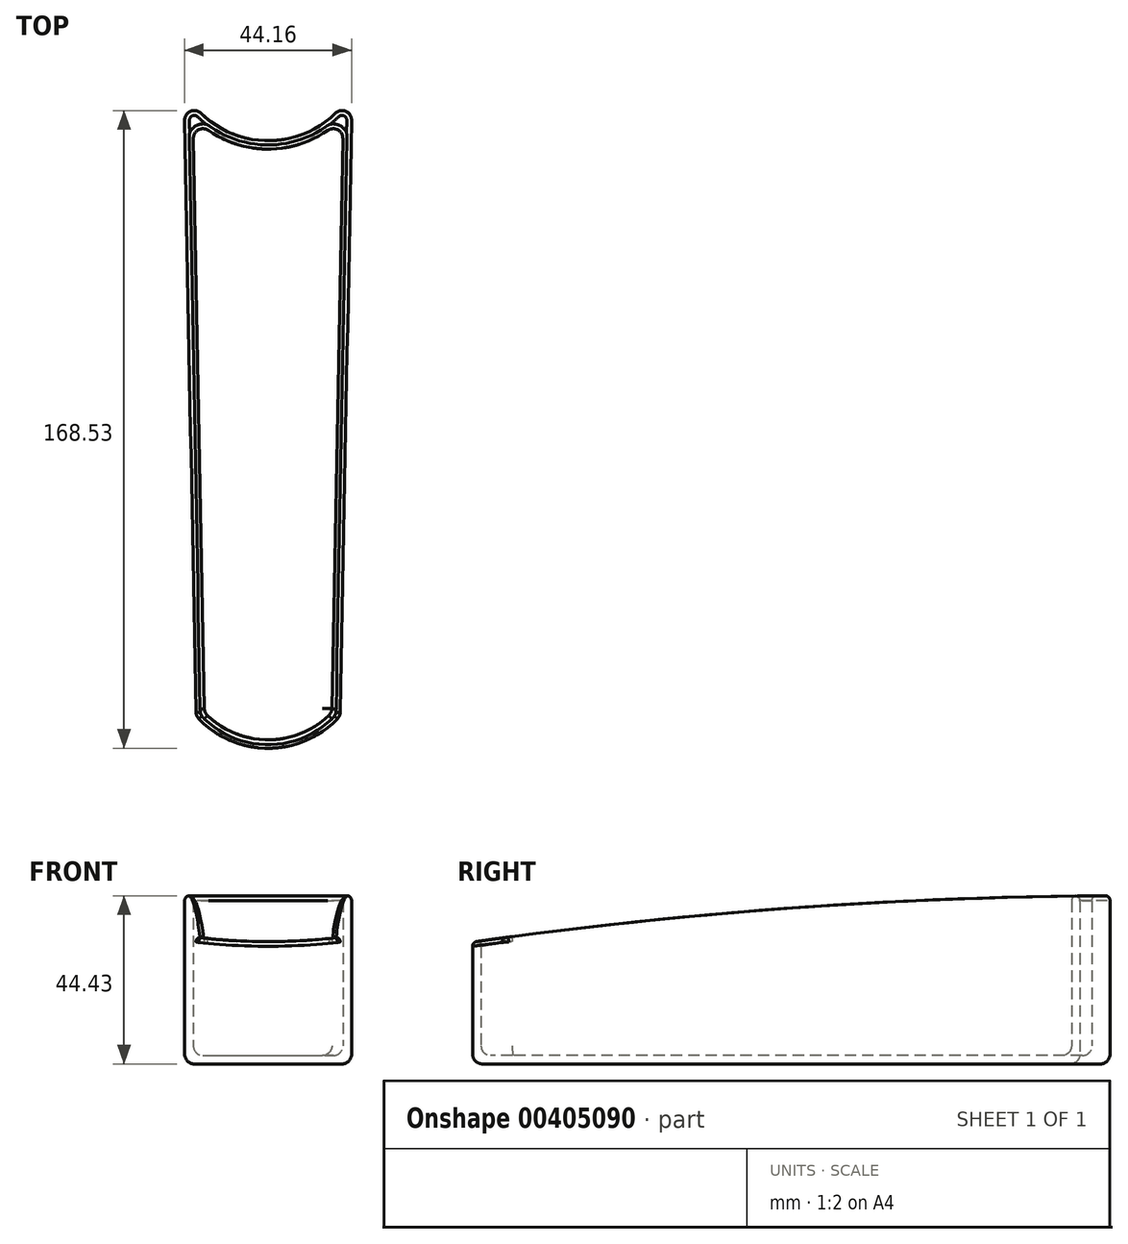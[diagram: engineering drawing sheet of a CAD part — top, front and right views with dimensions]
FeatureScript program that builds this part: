
annotation { "Feature Type Name" : "Feature", "Feature Type Description" : "" }
export const myFeature = defineFeature(function(context is Context, id is Id, definition is map)
    precondition{}
    {
        {
            var Q0;
            Q0=qCreatedBy(makeId("Top.planeOp"),FACE);
            var sketch = newSketch(context, id + "F0", { "sketchPlane" : qUnion([Q0])});
            skLineSegment(sketch, "E0", {"start": v(0, 76.2) * mm, "end": v(0, -76.2) * mm, "construction": true});
            skLineSegment(sketch, "E1", {"start": v(-22.23, 63.47) * mm, "end": v(0, 63.47) * mm, "construction": true});
            skLineSegment(sketch, "E2", {"start": v(0, -101.6) * mm, "end": v(-19.05, -101.6) * mm, "construction": true});
            skLineSegment(sketch, "E3", {"start": v(-22.23, 63.47) * mm, "end": v(-19.05, -101.6) * mm});
            skArc(sketch, "E4", {"start": v(-19.05, -101.6) * mm, "mid": v(-10.45, -107.95) * mm, "end": v(0, -110.2) * mm});
            skLineSegment(sketch, "E5", {"start": v(0, -110.2) * mm, "end": v(27.93, -110.2) * mm, "construction": true});
            skArc(sketch, "E6", {"start": v(-22.22, 63.47) * mm, "mid": v(-12.9, 53.89) * mm, "end": v(0, 50.37) * mm});
            skLineSegment(sketch, "E7", {"start": v(0, 50.37) * mm, "end": v(33.83, 50.37) * mm, "construction": true});
            skArc(sketch, "E8.MirrorCS", {"start": v(22.22, 63.47) * mm, "mid": v(12.9, 53.89) * mm, "end": v(0, 50.37) * mm});
            skLineSegment(sketch, "E9.MirrorCS", {"start": v(22.22, 63.47) * mm, "end": v(19.05, -101.6) * mm});
            skArc(sketch, "E10.MirrorCS", {"start": v(19.05, -101.6) * mm, "mid": v(10.45, -107.95) * mm, "end": v(0, -110.2) * mm});
            skArc(sketch, "E11.0", {"start": v(-19.54, 55.8) * mm, "mid": v(-10.55, 49.9) * mm, "end": v(0, 47.83) * mm, "construction": true});
            skArc(sketch, "E11.1", {"start": v(-16.53, -100.6) * mm, "mid": v(-8.99, -105.82) * mm, "end": v(0, -107.66) * mm, "construction": true});
            skArc(sketch, "E11.2", {"start": v(16.53, -100.6) * mm, "mid": v(8.99, -105.82) * mm, "end": v(0, -107.66) * mm, "construction": true});
            skLineSegment(sketch, "E11.3", {"start": v(-19.54, 55.8) * mm, "end": v(-16.53, -100.6) * mm, "construction": true});
            skLineSegment(sketch, "E11.4", {"start": v(19.54, 55.8) * mm, "end": v(16.53, -100.6) * mm, "construction": true});
            skArc(sketch, "E11.5", {"start": v(19.54, 55.8) * mm, "mid": v(10.55, 49.9) * mm, "end": v(0, 47.83) * mm, "construction": true});
            skCircle(sketch, "E12", {"center": v(0, 76.2) * mm, "radius": 22.86 * mm, "construction": true});
            skSolve(sketch);
        }
        {
            var Q0;
            Q0 = qSketchRegion(id + "F0", true);
            extrude(context, id + "F1", {"entities" : qUnion([Q0]), "depth" : 50.8 * mm, "offsetDistance" : 25.4 * mm});
        }
        {
            var Q0;
            Q0=qCreatedBy(makeId("Right.planeOp"),FACE);
            var sketch = newSketch(context, id + "F2", { "sketchPlane" : qUnion([Q0])});
            skArc(sketch, "E13", {"start": v(63.79, 44.45) * mm, "mid": v(-25.02, 41.27) * mm, "end": v(-113.37, 31.75) * mm});
            skLineSegment(sketch, "E14", {"start": v(63.79, 44.45) * mm, "end": v(63.79, 69.85) * mm});
            skLineSegment(sketch, "E15", {"start": v(63.79, 69.85) * mm, "end": v(-113.37, 69.85) * mm});
            skLineSegment(sketch, "E16", {"start": v(-113.37, 69.85) * mm, "end": v(-113.37, 31.75) * mm});
            skPoint(sketch, "E17.0", {"position": v(63.47, 0) * mm});
            skPoint(sketch, "E17.1", {"position": v(-110.2, 0) * mm});
            skLineSegment(sketch, "E18", {"start": v(63.79, 44.45) * mm, "end": v(76.14, 44.45) * mm, "construction": true});
            skSolve(sketch);
        }
        {
            var Q0;
            Q0=makeQuery(id+"F2.imprint","IMPRINT",FACE,{"disambiguationData":[TD([[makeQuery(id+"F2.imprint","IMPRINT",EDGE,{"derivedFrom":sQuery(id+"F2.wireOp",EDGE,"E13")}),-1.0]])]});
            extrude(context, id + "F3", {"entities" : qUnion([Q0]), "operationType" : NewBodyOperationType.REMOVE, "endBound" : BoundingType.THROUGH_ALL, "oppositeDirection" : true, "depth" : 25.4 * mm, "offsetDistance" : 25.4 * mm, "hasSecondDirection" : true, "secondDirectionBound" : SecondDirectionBoundingType.THROUGH_ALL, "secondDirectionOppositeDirection" : false, "secondDirectionDepth" : 25.4 * mm});
        }
        {
            var Q0;
            Q0=makeQuery(id+"F3.boolean.opBoolean","COPY",FACE,{"derivedFrom":makeQuery(id+"F3.opExtrude","SWEPT_FACE",FACE,{"disambiguationData":[OSD([sQuery(id+"F2.wireOp",EDGE,"E13")])]})});
            shell(context, id + "F4", {"entities" : qUnion([Q0]), "thickness" : 2.22 * mm});
        }
        {
            var Q0;
            Q0=makeQuery(id+"F4.opShell","OFFSET_FACE",FACE,{"disambiguationData":[OSD([sQuery(id+"F0.wireOp",EDGE,"E3"),sQuery(id+"F0.wireOp",EDGE,"E4"),sQuery(id+"F0.wireOp",EDGE,"E6"),sQuery(id+"F0.wireOp",EDGE,"E8.MirrorCS"),sQuery(id+"F0.wireOp",EDGE,"E9.MirrorCS"),sQuery(id+"F0.wireOp",EDGE,"E10.MirrorCS")])]});
            var Q1;
            Q1=makeQuery(id+"F4.opShell","OFFSET_EDGE",EDGE,{"disambiguationData":[OSD([sQuery(id+"F0.wireOp",EDGE,"E3"),sQuery(id+"F0.wireOp",EDGE,"E4")])]});
            var Q2;
            Q2=makeQuery(id+"F4.opShell","OFFSET_EDGE",EDGE,{"disambiguationData":[OSD([sQuery(id+"F0.wireOp",EDGE,"E3"),sQuery(id+"F0.wireOp",EDGE,"E6")])]});
            var Q3;
            Q3=makeQuery(id+"F4.opShell","OFFSET_EDGE",EDGE,{"disambiguationData":[OSD([sQuery(id+"F0.wireOp",EDGE,"E8.MirrorCS"),sQuery(id+"F0.wireOp",EDGE,"E9.MirrorCS")])]});
            var Q4;
            Q4=makeQuery(id+"F4.opShell","OFFSET_EDGE",EDGE,{"disambiguationData":[OSD([sQuery(id+"F0.wireOp",EDGE,"E9.MirrorCS"),sQuery(id+"F0.wireOp",EDGE,"E10.MirrorCS")])]});
            var Q5;
            Q5=makeQuery(id+"F1.opExtrude","SWEPT_EDGE",EDGE,{"disambiguationData":[OSD([sQuery(id+"F0.wireOp",EDGE,"E3"),sQuery(id+"F0.wireOp",EDGE,"E6")])]});
            var Q6;
            Q6=makeQuery(id+"F1.opExtrude","SWEPT_EDGE",EDGE,{"disambiguationData":[OSD([sQuery(id+"F0.wireOp",EDGE,"E8.MirrorCS"),sQuery(id+"F0.wireOp",EDGE,"E9.MirrorCS")])]});
            var Q7;
            Q7=makeQuery(id+"F1.opExtrude","CAP_FACE",FACE,{"disambiguationData":[OSD([sQuery(id+"F0.wireOp",EDGE,"E3"),sQuery(id+"F0.wireOp",EDGE,"E4"),sQuery(id+"F0.wireOp",EDGE,"E6"),sQuery(id+"F0.wireOp",EDGE,"E8.MirrorCS"),sQuery(id+"F0.wireOp",EDGE,"E9.MirrorCS"),sQuery(id+"F0.wireOp",EDGE,"E10.MirrorCS")])],"isStart":true});
            var Q8;
            Q8=makeQuery(id+"F1.opExtrude","SWEPT_EDGE",EDGE,{"disambiguationData":[OSD([sQuery(id+"F0.wireOp",EDGE,"E3"),sQuery(id+"F0.wireOp",EDGE,"E4")])]});
            var Q9;
            Q9=makeQuery(id+"F1.opExtrude","SWEPT_EDGE",EDGE,{"disambiguationData":[OSD([sQuery(id+"F0.wireOp",EDGE,"E9.MirrorCS"),sQuery(id+"F0.wireOp",EDGE,"E10.MirrorCS")])]});
            fillet(context, id + "F5", {"entities" : qUnion([Q0, Q1, Q2, Q3, Q4, Q5, Q6, Q7, Q8, Q9]), "tangentPropagation" : true, "radius" : 2.54 * mm, "defaultsChanged" : false, "vertexSettings" : [], "allowEdgeOverflow" : false});
        }
        {
            var Q0;
            Q0=makeQuery(id+"F3.boolean.opBoolean","COPY",FACE,{"derivedFrom":makeQuery(id+"F3.opExtrude","SWEPT_FACE",FACE,{"disambiguationData":[OSD([sQuery(id+"F2.wireOp",EDGE,"E13")])]})});
            fillet(context, id + "F6", {"entities" : qUnion([Q0]), "tangentPropagation" : true, "radius" : 1.27 * mm, "defaultsChanged" : true, "vertexSettings" : [], "allowEdgeOverflow" : false});
        }
    });
